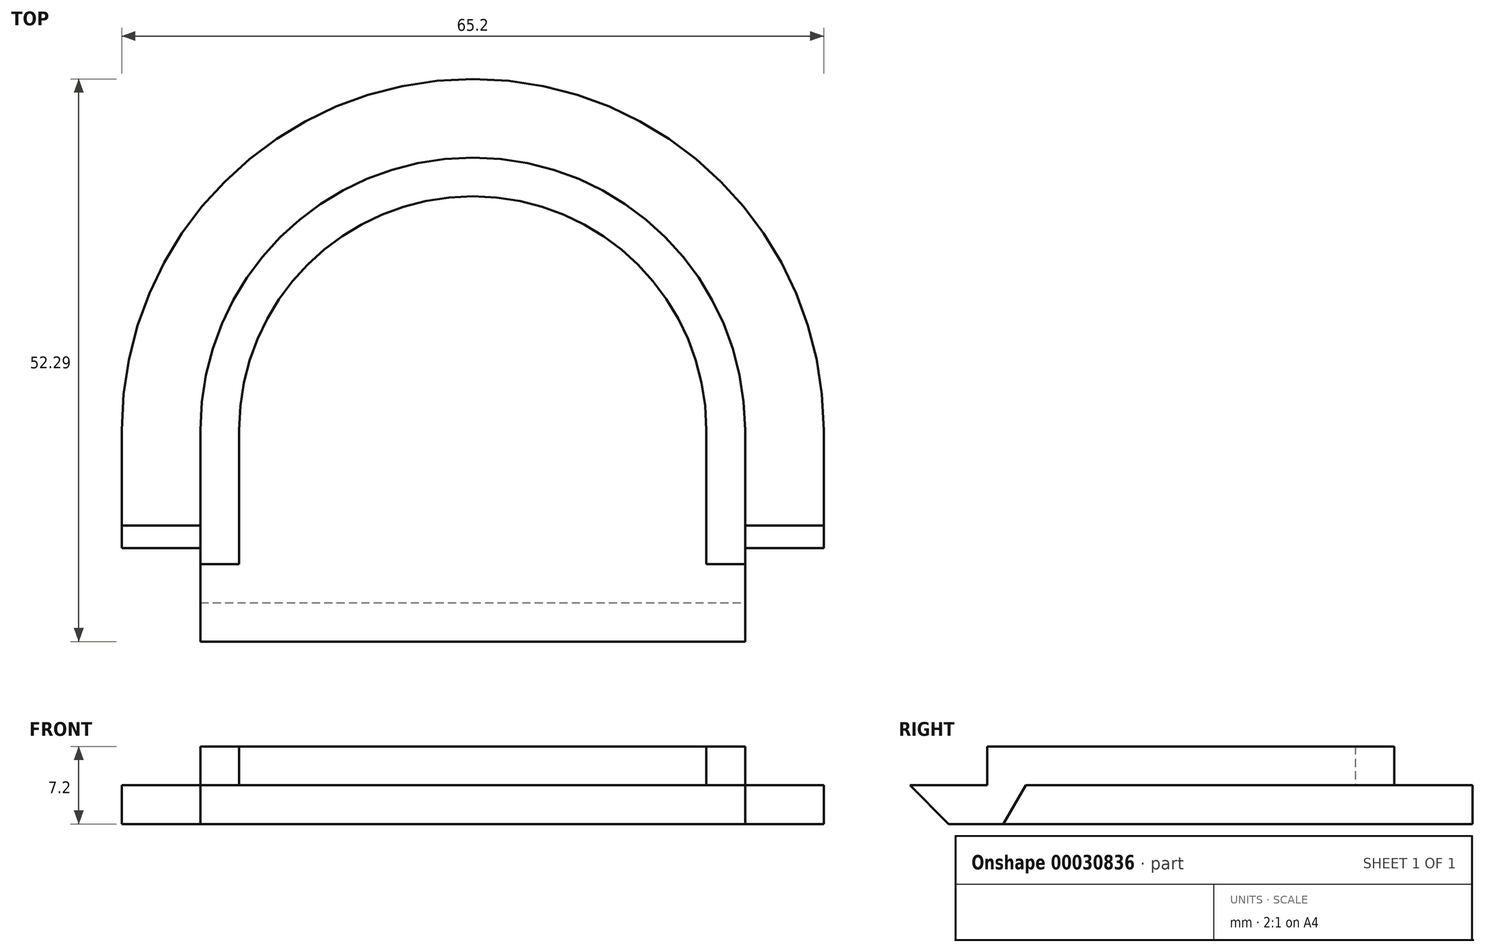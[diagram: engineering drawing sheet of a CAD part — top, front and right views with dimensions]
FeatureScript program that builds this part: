
annotation { "Feature Type Name" : "Feature", "Feature Type Description" : "" }
export const myFeature = defineFeature(function(context is Context, id is Id, definition is map)
    precondition{}
    {
        {
            var Q0;
            Q0=qCreatedBy(makeId("Top.planeOp"),FACE);
            var sketch = newSketch(context, id + "F0", { "sketchPlane" : qUnion([Q0])});
            skLineSegment(sketch, "E0", {"start": v(-32.6, -11) * mm, "end": v(-25.3, -11) * mm});
            skLineSegment(sketch, "E1", {"start": v(-25.3, -11) * mm, "end": v(-25.3, -21) * mm});
            skLineSegment(sketch, "E2", {"start": v(-25.3, -21) * mm, "end": v(25.3, -21) * mm});
            skLineSegment(sketch, "E3", {"start": v(25.3, -21) * mm, "end": v(25.3, -11) * mm});
            skLineSegment(sketch, "E4", {"start": v(25.3, -11) * mm, "end": v(32.6, -11) * mm});
            skLineSegment(sketch, "E5", {"start": v(32.6, -11) * mm, "end": v(32.6, 0) * mm});
            skLineSegment(sketch, "E6", {"start": v(-32.6, -11) * mm, "end": v(-32.6, 0) * mm});
            skArc(sketch, "E7", {"start": v(32.6, 0) * mm, "mid": v(0, 32.6) * mm, "end": v(-32.6, 0) * mm});
            skPoint(sketch, "E8", {"position": v(0, 32.6) * mm});
            skSolve(sketch);
        }
        {
            var Q0;
            Q0 = qSketchRegion(id + "F0", true);
            extrude(context, id + "F1", {"entities" : qUnion([Q0]), "depth" : 3.6 * mm});
        }
        {
            var Q0;
            Q0=makeQuery(id+"F1.opExtrude","SWEPT_FACE",FACE,{"disambiguationData":[OSD([sQuery(id+"F0.wireOp",EDGE,"E5")])]});
            var sketch = newSketch(context, id + "F2", { "sketchPlane" : qUnion([Q0])});
            skLineSegment(sketch, "E9", {"start": v(-11, 3.6) * mm, "end": v(-11, 0) * mm});
            skLineSegment(sketch, "E10", {"start": v(-11, 0) * mm, "end": v(-8.9, 3.6) * mm});
            skLineSegment(sketch, "E11", {"start": v(-8.9, 3.6) * mm, "end": v(-11, 3.6) * mm});
            skSolve(sketch);
        }
        {
            var Q0;
            Q0 = qSketchRegion(id + "F2", true);
            var Q1;
            Q1=makeQuery(id+"F1.opExtrude","SWEPT_FACE",FACE,{"disambiguationData":[OSD([sQuery(id+"F0.wireOp",EDGE,"E3")])]});
            extrude(context, id + "F3", {"entities" : qUnion([Q0]), "operationType" : NewBodyOperationType.REMOVE, "endBound" : BoundingType.UP_TO_SURFACE, "oppositeDirection" : true, "endBoundEntityFace" : qUnion([Q1]), "depth" : 25 * mm});
        }
        {
            var Q0;
            Q0=makeQuery(id+"F1.opExtrude","SWEPT_FACE",FACE,{"disambiguationData":[OSD([sQuery(id+"F0.wireOp",EDGE,"E6")])]});
            var sketch = newSketch(context, id + "F4", { "sketchPlane" : qUnion([Q0])});
            skLineSegment(sketch, "E12.0", {"start": v(11, 3.6) * mm, "end": v(11, 0) * mm});
            skLineSegment(sketch, "E12.1", {"start": v(11, 0) * mm, "end": v(8.9, 3.6) * mm});
            skLineSegment(sketch, "E12.2", {"start": v(8.9, 3.6) * mm, "end": v(11, 3.6) * mm});
            skSolve(sketch);
        }
        {
            var Q0;
            Q0 = qSketchRegion(id + "F4", true);
            var Q1;
            Q1=makeQuery(id+"F1.opExtrude","SWEPT_FACE",FACE,{"disambiguationData":[OSD([sQuery(id+"F0.wireOp",EDGE,"E1")])]});
            extrude(context, id + "F5", {"entities" : qUnion([Q0]), "operationType" : NewBodyOperationType.REMOVE, "endBound" : BoundingType.UP_TO_SURFACE, "oppositeDirection" : true, "endBoundEntityFace" : qUnion([Q1]), "depth" : 25 * mm});
        }
        {
            var Q0;
            Q0=makeQuery(id+"F1.opExtrude","CAP_FACE",FACE,{"disambiguationData":[OSD([sQuery(id+"F0.wireOp",EDGE,"E0"),sQuery(id+"F0.wireOp",EDGE,"E1"),sQuery(id+"F0.wireOp",EDGE,"E2"),sQuery(id+"F0.wireOp",EDGE,"E3"),sQuery(id+"F0.wireOp",EDGE,"E4"),sQuery(id+"F0.wireOp",EDGE,"E5"),sQuery(id+"F0.wireOp",EDGE,"E6"),sQuery(id+"F0.wireOp",EDGE,"E7")])],"isStart":false});
            var sketch = newSketch(context, id + "F6", { "sketchPlane" : qUnion([Q0])});
            skLineSegment(sketch, "E13", {"start": v(-25.3, -12.5) * mm, "end": v(-25.3, 0) * mm});
            skLineSegment(sketch, "E14", {"start": v(25.3, -12.5) * mm, "end": v(25.3, 0) * mm});
            skArc(sketch, "E15", {"start": v(25.3, 0) * mm, "mid": v(0, 25.3) * mm, "end": v(-25.3, 0) * mm});
            skLineSegment(sketch, "E16", {"start": v(-25.3, -12.5) * mm, "end": v(-21.7, -12.5) * mm});
            skLineSegment(sketch, "E17", {"start": v(-21.7, -12.5) * mm, "end": v(-21.7, 0) * mm});
            skLineSegment(sketch, "E18", {"start": v(25.3, -12.5) * mm, "end": v(21.7, -12.5) * mm});
            skLineSegment(sketch, "E19", {"start": v(21.7, -12.5) * mm, "end": v(21.7, 0) * mm});
            skArc(sketch, "E20", {"start": v(21.7, 0) * mm, "mid": v(0, 21.7) * mm, "end": v(-21.7, 0) * mm});
            skSolve(sketch);
        }
        {
            var Q0;
            Q0 = qSketchRegion(id + "F6", true);
            extrude(context, id + "F7", {"entities" : qUnion([Q0]), "operationType" : NewBodyOperationType.ADD, "depth" : 3.6 * mm});
        }
        {
            var Q0;
            Q0=makeQuery(id+"F7.boolean.opBoolean","MERGE",FACE,{"derivedFrom":[makeQuery(id+"F3.boolean.opBoolean","MERGE",FACE,{"derivedFrom":[makeQuery(id+"F1.opExtrude","SWEPT_FACE",FACE,{"disambiguationData":[OSD([sQuery(id+"F0.wireOp",EDGE,"E3")])]}),makeQuery(id+"F3.opExtrude","CAP_FACE",FACE,{"disambiguationData":[OSD([sQuery(id+"F2.wireOp",EDGE,"E9"),sQuery(id+"F2.wireOp",EDGE,"E10"),sQuery(id+"F2.wireOp",EDGE,"E11")])],"isStart":false})]}),makeQuery(id+"F7.opExtrude","SWEPT_FACE",FACE,{"disambiguationData":[OSD([sQuery(id+"F6.wireOp",EDGE,"E14")])]})]});
            var sketch = newSketch(context, id + "F8", { "sketchPlane" : qUnion([Q0])});
            skLineSegment(sketch, "E21", {"start": v(-21, 3.6) * mm, "end": v(-21, 0) * mm});
            skLineSegment(sketch, "E22", {"start": v(-21, 0) * mm, "end": v(-16.1, 0) * mm});
            skLineSegment(sketch, "E23", {"start": v(-16.1, 0) * mm, "end": v(-19.7, 3.6) * mm});
            skLineSegment(sketch, "E24", {"start": v(-19.7, 3.6) * mm, "end": v(-21, 3.6) * mm});
            skSolve(sketch);
        }
        {
            var Q0;
            Q0 = qSketchRegion(id + "F8", true);
            extrude(context, id + "F9", {"entities" : qUnion([Q0]), "operationType" : NewBodyOperationType.REMOVE, "endBound" : BoundingType.THROUGH_ALL, "oppositeDirection" : true, "depth" : 25 * mm});
        }
    });
